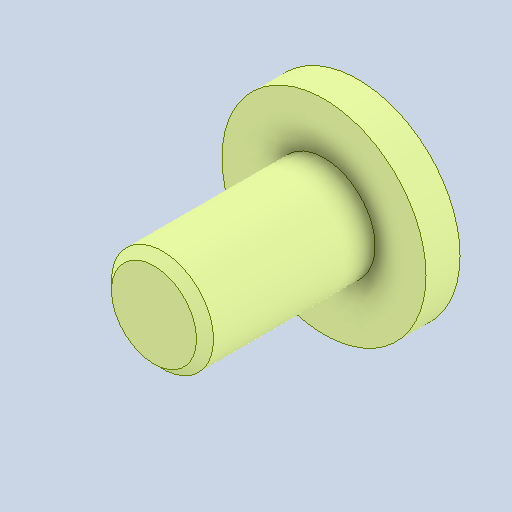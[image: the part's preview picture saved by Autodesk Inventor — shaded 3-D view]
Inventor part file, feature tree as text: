
AUTODESK INVENTOR PART (.ipt)
format: ipt  version: 2022 (Build 260153000, 153)  size: 112,128 bytes
history: native  units: in
note: dims shown in document units (in); Inventor stores cm internally (conversion verified against a paired STEP export)
features: extrude x2, sketch x2, chamfer x1
ambient origin geometry x8: Origin, YZ Plane, XZ Plane, XY Plane, X Axis, Y Axis, Z Axis, Center Point
bodies: Solid1 (feature_tree)
feature tree (5):
  extrude  "Extrusion1"  Depth=0.0787in TaperAngle=0.0deg
  extrude  "Extrusion2"  Depth=0.3937in TaperAngle=0.0deg
  chamfer  "Chamfer1"  Distance=0.0787in Angle=45.0deg
  sketch  "Sketch1"  dims[d0=0.4724in d1=0.0787in d2=0.0in]
  sketch  "Sketch2"  dims[d3=0.2362in d4=0.3937in d5=0.0in d6=0.0197in d7=0.0787in d8=45.0deg]
